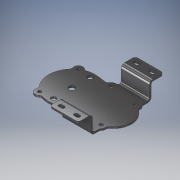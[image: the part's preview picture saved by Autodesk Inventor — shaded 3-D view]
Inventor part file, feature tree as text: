
AUTODESK INVENTOR PART (.ipt)
format: ipt  version: 2017 (Build 210142000, 142)  size: 343,040 bytes
history: native  units: mm
features: extrude x5, sketch x5, fillet x4, other x1, plane x1, mirror x1
ambient origin geometry x8: Origin, YZ Plane, XZ Plane, XY Plane, X Axis, Y Axis, Z Axis, Center Point
bodies: Body1 (feature_tree)
feature tree (17):
  other  "Sólido1"
  extrude  "Extrusión1"  Depth=88.9mm
  plane  "Plano de trabajo1"
  extrude  "Extrusión3"  Depth=22.225mm
  fillet  "Empalme3"  Radius=22.225mm
  fillet  "Empalme4"  Radius=22.225mm
  extrude  "Extrusión4"  Depth=22.225mm
  fillet  "Empalme5"  [1 undecoded]
  mirror  "Simetría1"
  extrude  "Extrusión2"  Depth=4.445mm TaperAngle=0.0deg
  fillet  "Empalme6"  Radius=8.4328mm
  extrude  "Extrusión5"  Depth=6.35mm
  sketch  "Boceto1"  dims[d0=114.3mm d1=88.9mm]
  sketch  "Boceto2"  dims[d2=203.2mm d3=22.225mm d4=22.225mm d7=22.225mm]
  sketch  "Boceto3"  dims[d8=22.225mm d11=22.225mm d13=0.0mm]
  sketch  "Boceto4"  dims[d14=22.225mm d16=4.445mm d17=0.0mm d18=8.4328mm]
  sketch  "Boceto5"  dims[d19=8.4328mm d20=8.4328mm d21=8.4328mm d22=8.4328mm d23=8.4328mm d24=25.4mm d25=0.0mm d27=50.8mm d28=4.445mm d29=4.445mm d30=69.85mm d31=44.45mm d32=104.775mm d33=69.85mm d34=0.0mm d35=31.75mm d36=31.75mm d37=44.45mm d38=44.45mm d39=12.7mm d40=12.7mm d42=4.445mm d43=8.89mm d44=8.382mm d45=8.382mm d46=14.6812mm d47=8.5344mm d48=12.7254mm d49=8.382mm d50=8.382mm d51=14.6812mm d52=8.5344mm d53=12.7254mm d54=69.85mm d55=0.0mm d56=6.35mm d57=6.35mm d58=14.2875mm d59=45.0mm d60=45.0mm d61=12.0mm d62=12.0mm d63=25.4mm d64=0.0mm]
note: 1 required parameter value undecoded (feature->parameter linkage not recoverable at this tier; creation-order binding heuristic only, values carry confidence <= 0.55)
